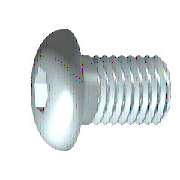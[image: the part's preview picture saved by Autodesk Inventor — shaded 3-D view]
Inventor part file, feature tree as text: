
AUTODESK INVENTOR PART (.ipt)
format: ipt  version: 2015 (Build 190159000, 159)  size: 199,680 bytes
history: native  units: mm (DEFAULTED — no unit token found)
features: sketch x2, extrude x1, plane x1, fillet x1
ambient origin geometry x7: Origin, YZ Plane, XY Plane, X Axis, Y Axis, Z Axis, Center Point
bodies: Solid1 (feature_tree), Body (feature_tree)
feature tree (5):
  extrude  "Slot"  Depth=2.2098mm
  plane  "Work Plane1"
  fillet  "Fillet2"  Radius=2.2098mm
  sketch  "Sketch1"  dims[d1=7.93476mm d2=1.59014mm d3=2.2098mm]
  sketch  "Sketch2"  dims[d4=1.3208mm d5=60.0deg d6=4.1656mm d7=4.1656mm d8=2.756963mm d9=7.9248mm d10=90.0deg d11=10.0mm d12=0.0mm d13=7.93476mm d14=0.0mm d15=0.486918mm d16=0.486918mm d17=1.9558mm d19=0.0mm d26=9.525mm d27=45.0deg d28=0.0mm d29=0.0mm d30=0.1mm]
